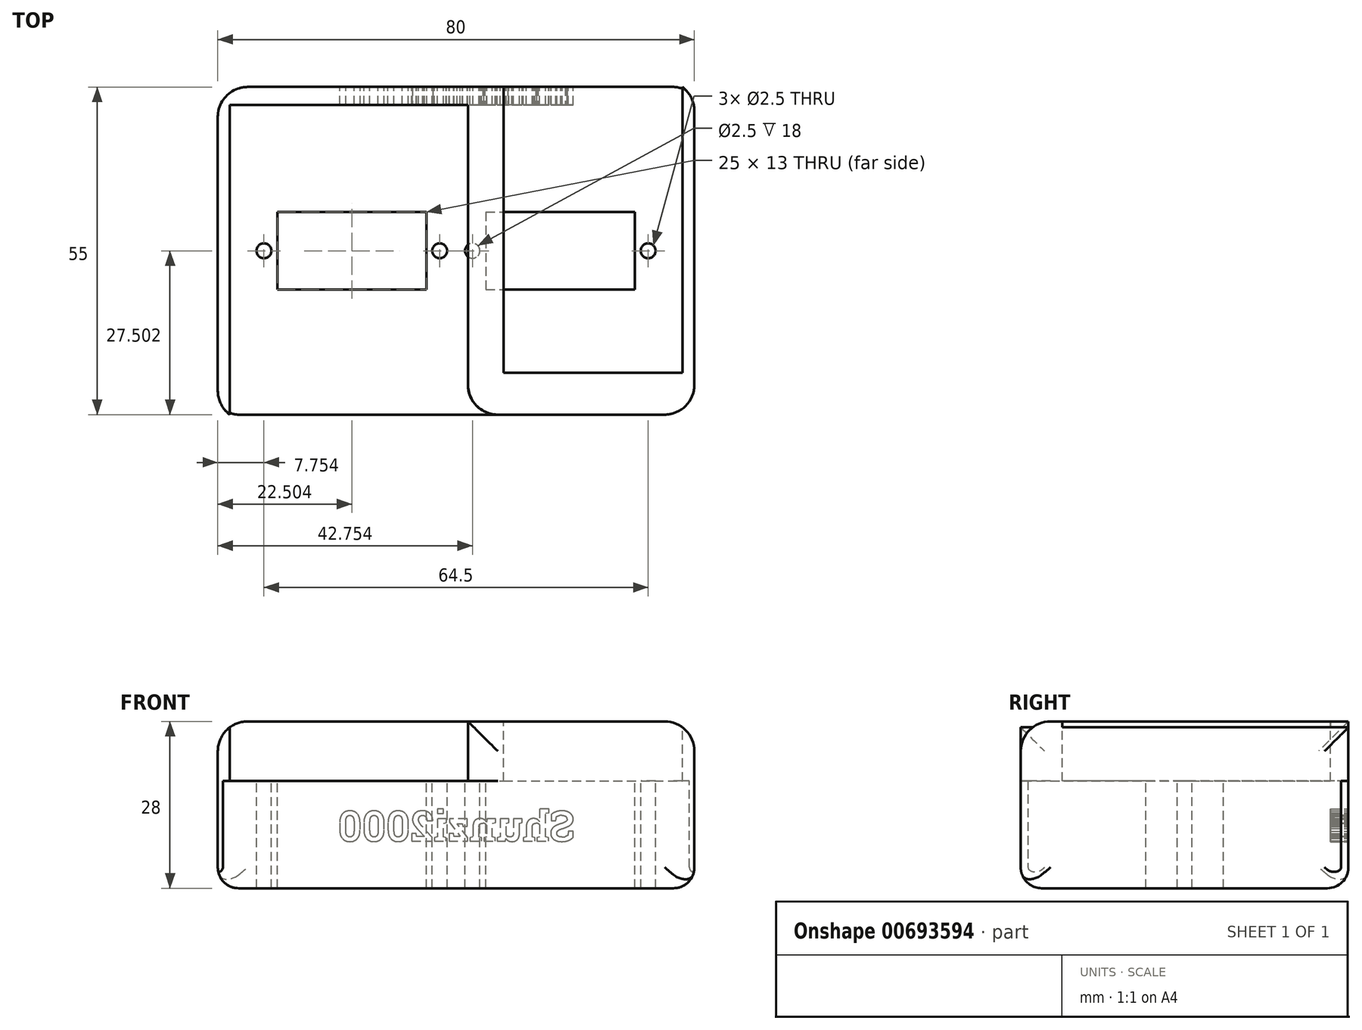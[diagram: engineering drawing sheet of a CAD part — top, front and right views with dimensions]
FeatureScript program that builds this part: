
annotation { "Feature Type Name" : "Feature", "Feature Type Description" : "" }
export const myFeature = defineFeature(function(context is Context, id is Id, definition is map)
    precondition{}
    {
        {
            var Q0;
            Q0=qCreatedBy(makeId("Top.planeOp"),FACE);
            var sketch = newSketch(context, id + "F0", { "sketchPlane" : qUnion([Q0])});
            skLineSegment(sketch, "E0.bottom", {"start": v(-39.96, 64.12) * mm, "end": v(40.04, 64.12) * mm});
            skLineSegment(sketch, "E0.top", {"start": v(-39.96, 9.12) * mm, "end": v(40.04, 9.12) * mm});
            skLineSegment(sketch, "E0.left", {"start": v(-39.96, 64.12) * mm, "end": v(-39.96, 9.12) * mm});
            skLineSegment(sketch, "E0.right", {"start": v(40.04, 64.12) * mm, "end": v(40.04, 9.12) * mm});
            skSolve(sketch);
        }
        {
            var Q0;
            Q0 = qSketchRegion(id + "F0", true);
            extrude(context, id + "F1", {"entities" : qUnion([Q0]), "depth" : 18 * mm, "offsetDistance" : 25 * mm});
        }
        {
            var Q0;
            Q0=makeQuery(id+"F1.opExtrude","CAP_FACE",FACE,{"disambiguationData":[OSD([sQuery(id+"F0.wireOp",EDGE,"E0.bottom"),sQuery(id+"F0.wireOp",EDGE,"E0.top"),sQuery(id+"F0.wireOp",EDGE,"E0.left"),sQuery(id+"F0.wireOp",EDGE,"E0.right")])],"isStart":false});
            var sketch = newSketch(context, id + "F2", { "sketchPlane" : qUnion([Q0])});
            skLineSegment(sketch, "E1.bottom", {"start": v(-29.96, 43.12) * mm, "end": v(-4.96, 43.12) * mm});
            skLineSegment(sketch, "E1.top", {"start": v(-29.96, 30.12) * mm, "end": v(-4.96, 30.12) * mm});
            skLineSegment(sketch, "E1.left", {"start": v(-29.96, 43.12) * mm, "end": v(-29.96, 30.12) * mm});
            skLineSegment(sketch, "E1.right", {"start": v(-4.96, 43.12) * mm, "end": v(-4.96, 30.12) * mm});
            skLineSegment(sketch, "E2.bottom", {"start": v(5.04, 43.12) * mm, "end": v(30.04, 43.12) * mm});
            skLineSegment(sketch, "E2.top", {"start": v(5.04, 30.12) * mm, "end": v(30.04, 30.12) * mm});
            skLineSegment(sketch, "E2.left", {"start": v(5.04, 43.12) * mm, "end": v(5.04, 30.12) * mm});
            skLineSegment(sketch, "E2.right", {"start": v(30.04, 43.12) * mm, "end": v(30.04, 30.12) * mm});
            skPoint(sketch, "E3.centerSnap0", {"position": v(30.04, 36.62) * mm});
            skSolve(sketch);
        }
        {
            var Q0;
            Q0=makeQuery(id+"F2.imprint","IMPRINT",FACE,{"disambiguationData":[TD([[makeQuery(id+"F2.imprint","IMPRINT",EDGE,{"derivedFrom":sQuery(id+"F2.wireOp",EDGE,"1aPVuin3-0Xc5-tuod-7RDE-PuBenJTeAqPK")}),1.0]])]});
            var Q1;
            Q1=makeQuery(id+"F2.imprint","IMPRINT",FACE,{"disambiguationData":[TD([[makeQuery(id+"F2.imprint","IMPRINT",EDGE,{"derivedFrom":sQuery(id+"F2.wireOp",EDGE,"E1.bottom")}),-1.0]])]});
            var Q2;
            Q2=makeQuery(id+"F2.imprint","IMPRINT",FACE,{"disambiguationData":[TD([[makeQuery(id+"F2.imprint","IMPRINT",EDGE,{"derivedFrom":sQuery(id+"F2.wireOp",EDGE,"xjLy5b8T-gbN8-G5ni-AalU-E65Pg9NjOUvA")}),1.0]])]});
            var Q3;
            Q3=makeQuery(id+"F2.imprint","IMPRINT",FACE,{"disambiguationData":[TD([[makeQuery(id+"F2.imprint","IMPRINT",EDGE,{"derivedFrom":sQuery(id+"F2.wireOp",EDGE,"CEXaiBpB-nmaS-9AR5-okoZ-Y2GbSp1F2Ydh")}),1.0]])]});
            var Q4;
            Q4=makeQuery(id+"F2.imprint","IMPRINT",FACE,{"disambiguationData":[TD([[makeQuery(id+"F2.imprint","IMPRINT",EDGE,{"derivedFrom":sQuery(id+"F2.wireOp",EDGE,"E2.bottom")}),-1.0]])]});
            var Q5;
            Q5=makeQuery(id+"F2.imprint","IMPRINT",FACE,{"disambiguationData":[TD([[makeQuery(id+"F2.imprint","IMPRINT",EDGE,{"derivedFrom":sQuery(id+"F2.wireOp",EDGE,"E3")}),1.0]])]});
            extrude(context, id + "F3", {"entities" : qUnion([Q0, Q1, Q2, Q3, Q4, Q5]), "operationType" : NewBodyOperationType.REMOVE, "endBound" : BoundingType.THROUGH_ALL, "oppositeDirection" : true, "depth" : 25 * mm, "offsetDistance" : 25 * mm});
        }
        {
            var Q0;
            Q0=makeQuery(id+"F1.opExtrude","SWEPT_FACE",FACE,{"disambiguationData":[OSD([sQuery(id+"F0.wireOp",EDGE,"E0.bottom")])]});
            var sketch = newSketch(context, id + "F4", { "sketchPlane" : qUnion([Q0])});
            skText(sketch, "E4", { "text": "Shunzi2000\n", "fontName": "RobotoSlab-Bold.ttf"});
            const initialGuessF4  = {"E4": [-0.02004, 0.00789, 1, 0, 0.00511]};
            skSetInitialGuess(sketch, initialGuessF4);
            skSolve(sketch);
        }
        {
            var Q0;
            Q0 = qSketchRegion(id + "F4", true);
            extrude(context, id + "F5", {"entities" : qUnion([Q0]), "operationType" : NewBodyOperationType.REMOVE, "oppositeDirection" : true, "depth" : 3 * mm, "offsetDistance" : 25 * mm});
        }
        {
            var Q0;
            Q0=makeQuery(id+"F1.opExtrude","CAP_EDGE",EDGE,{"disambiguationData":[OSD([sQuery(id+"F0.wireOp",EDGE,"E0.bottom")])],"isStart":true});
            var Q1;
            Q1=makeQuery(id+"F1.opExtrude","CAP_EDGE",EDGE,{"disambiguationData":[OSD([sQuery(id+"F0.wireOp",EDGE,"E0.right")])],"isStart":true});
            var Q2;
            Q2=makeQuery(id+"F1.opExtrude","CAP_EDGE",EDGE,{"disambiguationData":[OSD([sQuery(id+"F0.wireOp",EDGE,"E0.top")])],"isStart":true});
            var Q3;
            Q3=makeQuery(id+"F1.opExtrude","CAP_EDGE",EDGE,{"disambiguationData":[OSD([sQuery(id+"F0.wireOp",EDGE,"E0.left")])],"isStart":true});
            var Q4;
            Q4=makeQuery(id+"F1.opExtrude","SWEPT_EDGE",EDGE,{"disambiguationData":[OSD([sQuery(id+"F0.wireOp",EDGE,"E0.bottom"),sQuery(id+"F0.wireOp",EDGE,"E0.left")])]});
            var Q5;
            Q5=makeQuery(id+"F1.opExtrude","SWEPT_EDGE",EDGE,{"disambiguationData":[OSD([sQuery(id+"F0.wireOp",EDGE,"E0.top"),sQuery(id+"F0.wireOp",EDGE,"E0.left")])]});
            var Q6;
            Q6=makeQuery(id+"F1.opExtrude","SWEPT_EDGE",EDGE,{"disambiguationData":[OSD([sQuery(id+"F0.wireOp",EDGE,"E0.bottom"),sQuery(id+"F0.wireOp",EDGE,"E0.right")])]});
            var Q7;
            Q7=makeQuery(id+"F1.opExtrude","SWEPT_EDGE",EDGE,{"disambiguationData":[OSD([sQuery(id+"F0.wireOp",EDGE,"E0.top"),sQuery(id+"F0.wireOp",EDGE,"E0.right")])]});
            fillet(context, id + "F6", {"entities" : qUnion([Q0, Q1, Q2, Q3, Q4, Q5, Q6, Q7]), "radius" : 3.5 * mm, "tangentPropagation" : true, "allowEdgeOverflow" : false});
        }
        {
            var Q0;
            Q0=makeQuery(id+"F1.opExtrude","CAP_FACE",FACE,{"disambiguationData":[OSD([sQuery(id+"F0.wireOp",EDGE,"E0.bottom"),sQuery(id+"F0.wireOp",EDGE,"E0.top"),sQuery(id+"F0.wireOp",EDGE,"E0.left"),sQuery(id+"F0.wireOp",EDGE,"E0.right")])],"isStart":false});
            var sketch = newSketch(context, id + "F7", { "sketchPlane" : qUnion([Q0])});
            skCircle(sketch, "E5", {"center": v(-32.2, 36.62) * mm, "radius": 1.25 * mm});
            skCircle(sketch, "E6", {"center": v(-2.7, 36.62) * mm, "radius": 1.25 * mm});
            skCircle(sketch, "E7", {"center": v(2.8, 36.62) * mm, "radius": 1.25 * mm});
            skCircle(sketch, "E8", {"center": v(32.3, 36.62) * mm, "radius": 1.25 * mm});
            skSolve(sketch);
        }
        {
            var Q0;
            Q0 = qSketchRegion(id + "F7", true);
            extrude(context, id + "F8", {"entities" : qUnion([Q0]), "operationType" : NewBodyOperationType.REMOVE, "endBound" : BoundingType.THROUGH_ALL, "oppositeDirection" : true, "depth" : 25 * mm, "offsetDistance" : 25 * mm});
        }
        {
            var Q0;
            Q0=makeQuery(id+"F1.opExtrude","CAP_FACE",FACE,{"disambiguationData":[OSD([sQuery(id+"F0.wireOp",EDGE,"E0.bottom"),sQuery(id+"F0.wireOp",EDGE,"E0.top"),sQuery(id+"F0.wireOp",EDGE,"E0.left"),sQuery(id+"F0.wireOp",EDGE,"E0.right")])],"isStart":false});
            var sketch = newSketch(context, id + "F9", { "sketchPlane" : qUnion([Q0])});
            skLineSegment(sketch, "E9.bottom", {"start": v(-39.96, 64.12) * mm, "end": v(40.04, 64.12) * mm});
            skLineSegment(sketch, "E9.top", {"start": v(-39.96, 9.12) * mm, "end": v(40.04, 9.12) * mm});
            skLineSegment(sketch, "E9.left", {"start": v(-39.96, 64.12) * mm, "end": v(-39.96, 9.12) * mm});
            skLineSegment(sketch, "E9.right", {"start": v(40.04, 64.12) * mm, "end": v(40.04, 9.12) * mm});
            skSolve(sketch);
        }
        {
            var Q0;
            Q0 = qSketchRegion(id + "F9", true);
            extrude(context, id + "F10", {"entities" : qUnion([Q0]), "operationType" : NewBodyOperationType.ADD, "depth" : 10 * mm, "offsetDistance" : 25 * mm});
        }
        {
            var Q0;
            Q0=makeQuery(id+"F10.opExtrude","CAP_FACE",FACE,{"disambiguationData":[OSD([sQuery(id+"F9.wireOp",EDGE,"E9.bottom"),sQuery(id+"F9.wireOp",EDGE,"E9.top"),sQuery(id+"F9.wireOp",EDGE,"E9.left"),sQuery(id+"F9.wireOp",EDGE,"E9.right")])],"isStart":false});
            var sketch = newSketch(context, id + "F11", { "sketchPlane" : qUnion([Q0])});
            skLineSegment(sketch, "E10.bottom", {"start": v(-37.96, 9.12) * mm, "end": v(2.04, 9.12) * mm});
            skLineSegment(sketch, "E10.top", {"start": v(-37.96, 61.12) * mm, "end": v(2.04, 61.12) * mm});
            skLineSegment(sketch, "E10.left", {"start": v(-37.96, 9.12) * mm, "end": v(-37.96, 61.12) * mm});
            skLineSegment(sketch, "E10.right", {"start": v(2.04, 9.12) * mm, "end": v(2.04, 61.12) * mm});
            skLineSegment(sketch, "E11.bottom", {"start": v(8.04, 64.12) * mm, "end": v(38.04, 64.12) * mm});
            skLineSegment(sketch, "E11.top", {"start": v(8.04, 16.12) * mm, "end": v(38.04, 16.12) * mm});
            skLineSegment(sketch, "E11.left", {"start": v(8.04, 64.12) * mm, "end": v(8.04, 16.12) * mm});
            skLineSegment(sketch, "E11.right", {"start": v(38.04, 64.12) * mm, "end": v(38.04, 16.12) * mm});
            skSolve(sketch);
        }
        {
            var Q0;
            Q0 = qSketchRegion(id + "F11", true);
            extrude(context, id + "F12", {"entities" : qUnion([Q0]), "operationType" : NewBodyOperationType.REMOVE, "oppositeDirection" : true, "depth" : 10 * mm, "offsetDistance" : 25 * mm});
        }
        {
            var Q0;
            Q0=makeQuery(id+"F10.opExtrude","SWEPT_EDGE",EDGE,{"disambiguationData":[OSD([sQuery(id+"F9.wireOp",EDGE,"E9.top"),sQuery(id+"F9.wireOp",EDGE,"E9.right")])]});
            var Q1;
            Q1=makeQuery(id+"F10.opExtrude","SWEPT_EDGE",EDGE,{"disambiguationData":[OSD([sQuery(id+"F9.wireOp",EDGE,"E9.bottom"),sQuery(id+"F9.wireOp",EDGE,"E9.right")])]});
            var Q2;
            Q2=makeQuery(id+"F10.opExtrude","SWEPT_EDGE",EDGE,{"disambiguationData":[OSD([sQuery(id+"F9.wireOp",EDGE,"E9.bottom"),sQuery(id+"F9.wireOp",EDGE,"E9.left")])]});
            var Q3;
            Q3=makeQuery(id+"F12.boolean.opBoolean","COPY",EDGE,{"derivedFrom":makeQuery(id+"F12.opExtrude","SWEPT_EDGE",EDGE,{"disambiguationData":[OSD([sQuery(id+"F9.wireOp",EDGE,"E9.bottom"),sQuery(id+"F11.wireOp",EDGE,"E11.bottom"),sQuery(id+"F11.wireOp",EDGE,"E11.left")])]})});
            var Q4;
            Q4=makeQuery(id+"F10.opExtrude","SWEPT_EDGE",EDGE,{"disambiguationData":[OSD([sQuery(id+"F9.wireOp",EDGE,"E9.top"),sQuery(id+"F9.wireOp",EDGE,"E9.left")])]});
            var Q5;
            Q5=makeQuery(id+"F12.boolean.opBoolean","COPY",EDGE,{"derivedFrom":makeQuery(id+"F12.opExtrude","SWEPT_EDGE",EDGE,{"disambiguationData":[OSD([sQuery(id+"F9.wireOp",EDGE,"E9.top"),sQuery(id+"F11.wireOp",EDGE,"E10.bottom"),sQuery(id+"F11.wireOp",EDGE,"E10.right")])]})});
            var Q6;
            {var subQ0=sQuery(id+"F9.wireOp",EDGE,"E9.top");Q6=makeQuery(id+"F12.boolean.opBoolean","SPLIT",EDGE,{"disambiguationData":[TD([makeQuery(id+"F1.opExtrude","SWEPT_FACE",FACE,{"disambiguationData":[OSD([sQuery(id+"F0.wireOp",EDGE,"E0.right")])]})])],"derivedFrom":makeQuery(id+"F10.opExtrude","CAP_EDGE",EDGE,{"disambiguationData":[OSD([subQ0])],"isStart":false})});}
            var Q7;
            Q7=makeQuery(id+"F12.boolean.opBoolean","COPY",EDGE,{"derivedFrom":makeQuery(id+"F12.opExtrude","CAP_EDGE",EDGE,{"disambiguationData":[OSD([sQuery(id+"F11.wireOp",EDGE,"E10.right")])],"isStart":true})});
            var Q8;
            Q8=makeQuery(id+"F10.opExtrude","CAP_EDGE",EDGE,{"disambiguationData":[OSD([sQuery(id+"F9.wireOp",EDGE,"E9.right")])],"isStart":false});
            var Q9;
            Q9=makeQuery(id+"F10.opExtrude","CAP_EDGE",EDGE,{"disambiguationData":[OSD([sQuery(id+"F9.wireOp",EDGE,"E9.left")])],"isStart":false});
            fillet(context, id + "F13", {"entities" : qUnion([Q0, Q1, Q2, Q3, Q4, Q5, Q6, Q7, Q8, Q9]), "radius" : 5 * mm, "tangentPropagation" : true, "allowEdgeOverflow" : false});
        }
    });
